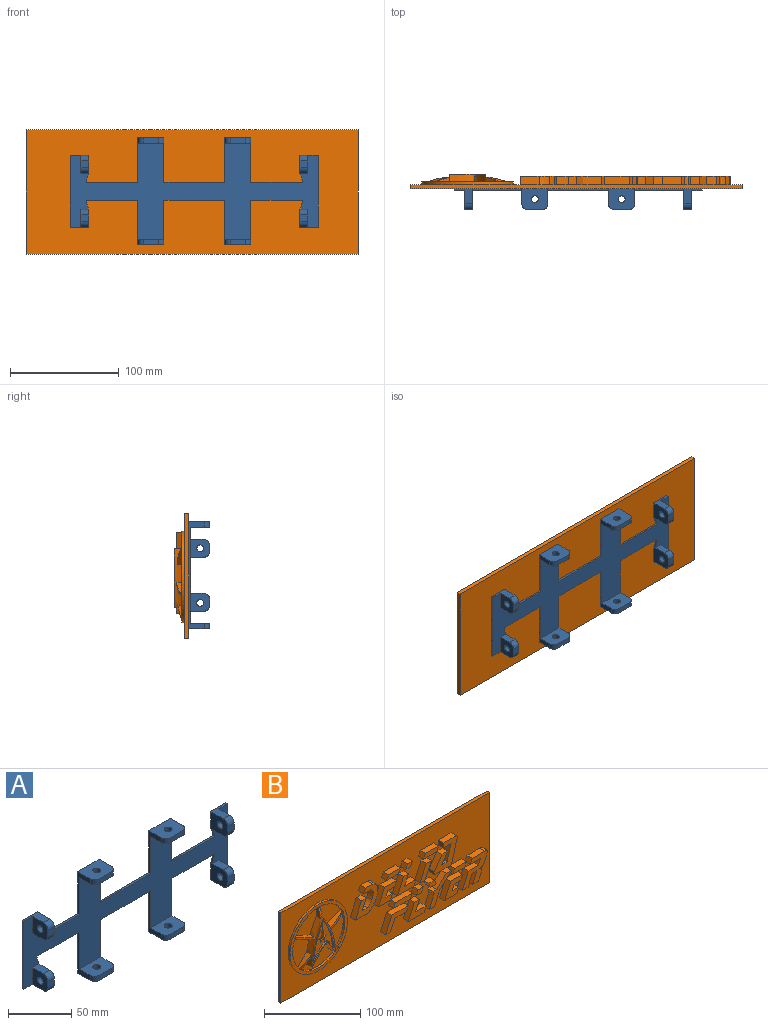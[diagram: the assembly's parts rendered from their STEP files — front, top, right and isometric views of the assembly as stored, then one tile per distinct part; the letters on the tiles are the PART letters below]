
ASSEMBLY  parts=2 mates=1
PART A: 78 faces, bbox 228.8x19.1x98.5 mm
  f0: plane 228.81x88.9mm, normal (0,-1,0), area 8492.5mm2, adj f1,f2,f3,f5,f6,f7,f9,f10
  f1: plane 40.81x13.97mm, normal (-1,0,0), area 131mm2, adj f0,f2,f34,f35,f36,f75
  f2: plane 47.52x1.78mm, normal (0,0,1), area 84.5mm2, adj f0,f1,f3,f35
  f3: cylinder r=50mm len=8.19mm, axis (0,1,0), area 15.1mm2, adj f0,f2,f4,f35
  f4: plane 19.05x16.45mm, normal (1,0,0), area 270.6mm2, adj f3,f5,f35,f45,f46,f57,f72,f73
  f5: plane 17.05x13.97mm, normal (0,0,1), area 116.4mm2, adj f0,f4,f6,f35,f44,f72
  f6: plane 66.15x1.78mm, normal (-1,0,0), area 117.6mm2, adj f0,f5,f7,f35
  f7: plane 17.05x13.97mm, normal (0,0,-1), area 116.4mm2, adj f0,f6,f8,f35,f48,f71
  f8: plane 19.05x16.45mm, normal (1,0,0), area 270.6mm2, adj f7,f9,f35,f47,f49,f56,f70,f71
  f9: cylinder r=50mm len=8.19mm, axis (0,1,0), area 15.1mm2, adj f0,f8,f10,f35
  f10: plane 47.52x1.78mm, normal (0,0,-1), area 84.5mm2, adj f0,f9,f11,f35
  f11: plane 40.81x13.97mm, normal (-1,0,0), area 131mm2, adj f0,f10,f12,f35,f38,f76
  f12: plane 24.02x19.05mm, normal (0,0,-1), area 414.8mm2, adj f11,f13,f35,f39,f60,f76,f77
  f13: plane 40.81x13.97mm, normal (1,0,0), area 131mm2, adj f0,f12,f14,f35,f38,f77
  f14: plane 55.89x1.78mm, normal (0,0,-1), area 99.4mm2, adj f0,f13,f15,f35
  f15: plane 40.81x13.97mm, normal (-1,0,0), area 131mm2, adj f0,f14,f16,f35,f40,f68
  f16: plane 24.02x19.05mm, normal (0,0,-1), area 414.8mm2, adj f15,f17,f35,f41,f59,f68,f69
  f17: plane 40.81x13.97mm, normal (1,0,0), area 131mm2, adj f0,f16,f18,f35,f40,f69
  f18: plane 47.77x1.78mm, normal (0,0,-1), area 84.9mm2, adj f0,f17,f19,f35
  f19: cylinder r=50mm len=8.19mm, axis (0,1,0), area 15.1mm2, adj f0,f18,f20,f35
  f20: plane 13.97x7.06mm, normal (0,0,1), area 86.5mm2, adj f0,f19,f21,f35,f52,f65
  f21: plane 19.05x16.45mm, normal (-1,0,0), area 270.6mm2, adj f20,f22,f35,f53,f54,f64,f65
  f22: plane 17.05x13.97mm, normal (0,0,-1), area 116.4mm2, adj f0,f21,f23,f35,f52,f64
  f23: plane 66.15x1.78mm, normal (1,0,0), area 117.6mm2, adj f0,f22,f24,f35
  f24: plane 17.05x13.97mm, normal (0,0,1), area 116.4mm2, adj f0,f23,f25,f35,f50,f62
  f25: plane 19.05x16.45mm, normal (-1,0,0), area 270.6mm2, adj f24,f26,f35,f51,f55,f62,f63
  f26: plane 13.97x7.06mm, normal (0,0,-1), area 86.5mm2, adj f0,f25,f27,f35,f50,f63
  f27: cylinder r=50mm len=8.19mm, axis (0,1,0), area 15.1mm2, adj f0,f26,f28,f35
  f28: plane 47.77x1.78mm, normal (0,0,1), area 84.9mm2, adj f0,f27,f29,f35
  f29: plane 40.81x13.97mm, normal (1,0,0), area 131mm2, adj f0,f28,f30,f35,f42,f66
  f30: plane 24.02x19.05mm, normal (0,0,1), area 414.8mm2, adj f29,f31,f35,f43,f58,f66,f67
  f31: plane 40.81x13.97mm, normal (-1,0,0), area 131mm2, adj f0,f30,f32,f35,f42,f67
  f32: plane 55.89x1.78mm, normal (0,0,1), area 99.4mm2, adj f0,f31,f33,f35
  f33: plane 40.81x13.97mm, normal (1,0,0), area 131mm2, adj f0,f32,f34,f35,f36,f74
  f34: plane 24.02x19.05mm, normal (0,0,1), area 414.8mm2, adj f1,f33,f35,f37,f61,f74,f75
  f35: plane 228.81x98.49mm, normal (0,1,0), area 9417.6mm2, adj f1,f2,f3,f4,f5,f6,f7,f8
  f36: plane 24.02x17.27mm, normal (0,0,-1), area 372.1mm2, adj f0,f1,f33,f37,f61,f74,f75
  f37: plane 13.86x4.8mm, normal (0,-1,0), area 66.5mm2, adj f34,f36,f74,f75
  f38: plane 24.02x17.27mm, normal (0,0,1), area 372.1mm2, adj f0,f11,f13,f39,f60,f76,f77
  f39: plane 13.86x4.8mm, normal (0,-1,0), area 66.5mm2, adj f12,f38,f76,f77
  f40: plane 24.02x17.27mm, normal (0,0,1), area 372.1mm2, adj f0,f15,f17,f41,f59,f68,f69
  f41: plane 13.86x4.8mm, normal (0,-1,0), area 66.5mm2, adj f16,f40,f68,f69
  f42: plane 24.02x17.27mm, normal (0,0,-1), area 372.1mm2, adj f0,f29,f31,f43,f58,f66,f67
  f43: plane 13.86x4.8mm, normal (0,-1,0), area 66.5mm2, adj f30,f42,f66,f67
  f44: plane 17.27x16.45mm, normal (-1,0,0), area 241.3mm2, adj f0,f5,f45,f46,f57,f72,f73
  f45: plane 12.19x7.06mm, normal (0,0,-1), area 86.1mm2, adj f0,f4,f44,f73
  f46: plane 7.06x6.29mm, normal (0,-1,0), area 44.4mm2, adj f4,f44,f72,f73
  f47: plane 12.19x7.06mm, normal (0,0,1), area 86.1mm2, adj f0,f8,f48,f70
  f48: plane 17.27x16.45mm, normal (-1,0,0), area 241.3mm2, adj f0,f7,f47,f49,f56,f70,f71
  f49: plane 7.06x6.29mm, normal (0,-1,0), area 44.4mm2, adj f8,f48,f70,f71
  f50: plane 17.27x16.45mm, normal (1,0,0), area 241.3mm2, adj f0,f24,f26,f51,f55,f62,f63
  f51: plane 7.06x6.29mm, normal (0,-1,0), area 44.4mm2, adj f25,f50,f62,f63
  f52: plane 17.27x16.45mm, normal (1,0,0), area 241.3mm2, adj f0,f20,f22,f53,f54,f64,f65
  f53: plane 7.06x6.29mm, normal (0,-1,0), area 44.4mm2, adj f21,f52,f64,f65
  f54: cylinder r=3.17mm len=7.06mm, axis (1,0,0), area 140.8mm2, adj f21,f52
  f55: cylinder r=3.17mm len=7.06mm, axis (1,0,0), area 140.8mm2, adj f25,f50
  f56: cylinder r=3.17mm len=7.06mm, axis (1,0,0), area 140.8mm2, adj f8,f48
  f57: cylinder r=3.17mm len=7.06mm, axis (1,0,0), area 140.8mm2, adj f4,f44
  f58: cylinder r=3.17mm len=6.35mm, axis (0,0,-1), area 95.7mm2, adj f30,f42
  f59: cylinder r=3.17mm len=6.35mm, axis (0,0,-1), area 95.7mm2, adj f16,f40
  f60: cylinder r=3.17mm len=6.35mm, axis (0,0,-1), area 95.7mm2, adj f12,f38
  f61: cylinder r=3.17mm len=6.35mm, axis (0,0,-1), area 95.7mm2, adj f34,f36
  f62: cylinder r=5.08mm len=7.06mm, axis (1,0,0), area 56.3mm2, adj f24,f25,f50,f51
  f63: cylinder r=5.08mm len=7.06mm, axis (-1,0,0), area 56.3mm2, adj f25,f26,f50,f51
  f64: cylinder r=5.08mm len=7.06mm, axis (-1,0,0), area 56.3mm2, adj f21,f22,f52,f53
  f65: cylinder r=5.08mm len=7.06mm, axis (1,0,0), area 56.3mm2, adj f20,f21,f52,f53
  f66: cylinder r=5.08mm len=5.08mm, axis (0,0,-1), area 38.3mm2, adj f29,f30,f42,f43
  f67: cylinder r=5.08mm len=5.08mm, axis (0,0,1), area 38.3mm2, adj f30,f31,f42,f43
  f68: cylinder r=5.08mm len=5.08mm, axis (0,0,1), area 38.3mm2, adj f15,f16,f40,f41
  f69: cylinder r=5.08mm len=5.08mm, axis (0,0,-1), area 38.3mm2, adj f16,f17,f40,f41
  f70: cylinder r=5.08mm len=7.06mm, axis (1,0,0), area 56.3mm2, adj f8,f47,f48,f49
  f71: cylinder r=5.08mm len=7.06mm, axis (-1,0,0), area 56.3mm2, adj f7,f8,f48,f49
  f72: cylinder r=5.08mm len=7.06mm, axis (1,0,0), area 56.3mm2, adj f4,f5,f44,f46
  f73: cylinder r=5.08mm len=7.06mm, axis (-1,0,0), area 56.3mm2, adj f4,f44,f45,f46
  f74: cylinder r=5.08mm len=5.08mm, axis (0,0,-1), area 38.3mm2, adj f33,f34,f36,f37
  f75: cylinder r=5.08mm len=5.08mm, axis (0,0,1), area 38.3mm2, adj f1,f34,f36,f37
  f76: cylinder r=5.08mm len=5.08mm, axis (0,0,1), area 38.3mm2, adj f11,f12,f38,f39
  f77: cylinder r=5.08mm len=5.08mm, axis (0,0,-1), area 38.3mm2, adj f12,f13,f38,f39
PART B: 198 faces, bbox 307.6x15x116 mm
  f0: plane 7.13x0.2mm, normal (-0.71,0,0.7), area 2mm2, adj f1,f14,f21,f181
  f1: plane 7.3x2.89mm, normal (-0.7,0,-0.71), area 28.9mm2, adj f0,f14,f21,f181
  f2: plane 10.27x10.11mm, normal (-0.7,0,-0.71), area 73mm2, adj f14,f22,f23,f174,f179
  f3: plane 12.48x12.3mm, normal (0.7,0,0.71), area 91.2mm2, adj f15,f22,f23,f31,f179
  f4: plane 23.9x11.42mm, normal (-0.41,0,0.91), area 146.5mm2, adj f16,f20,f24,f30,f179
  f5: plane 23.28x10.7mm, normal (0.41,0,-0.91), area 148mm2, adj f15,f20,f24,f31,f179
  f6: plane 12.38x6.44mm, normal (-1,0,0), area 60.4mm2, adj f12,f19,f25,f29,f178
  f7: plane 12.02x6.38mm, normal (1,0,0), area 58.2mm2, adj f16,f19,f25,f30,f179
  f8: plane 25.58x12.34mm, normal (0.41,0,0.91), area 157.2mm2, adj f12,f18,f26,f29,f178
  f9: plane 24.74x11.38mm, normal (-0.41,0,-0.91), area 159.1mm2, adj f13,f18,f26,f28,f178
  f10: plane 11.54x11.37mm, normal (0.7,0,-0.71), area 84.4mm2, adj f14,f17,f27,f174,f178
  f11: plane 14.14x13.93mm, normal (-0.7,0,0.71), area 105.9mm2, adj f13,f17,f27,f28,f178
  f12: plane 32.85x31.32mm, normal (0,-1,0), area 607.9mm2, adj f6,f8,f29,f178
  f13: plane 40.92x27.38mm, normal (0,-1,0), area 711.6mm2, adj f9,f11,f28,f178
  f14: plane 54.07x32.14mm, normal (0,-1,0), area 954.8mm2, adj f0,f1,f2,f10,f174,f178,f179,f181
  f15: plane 40.92x25.98mm, normal (0,-1,0), area 683.9mm2, adj f3,f5,f31,f179
  f16: plane 32.85x30.71mm, normal (0,-1,0), area 587.5mm2, adj f4,f7,f30,f179
  f17: revolved ~16.37x15.22mm, area 45.6mm2, adj f10,f11,f27,f178
  f18: revolved ~25.12x16.72mm, area 72.4mm2, adj f8,f9,f26,f178
  f19: revolved ~12.24x3.4mm, area 27.6mm2, adj f6,f7,f25,f178,f179
  f20: revolved ~23.71x15.5mm, area 65.7mm2, adj f4,f5,f24,f179
  f21: revolved ~3.16x3.11mm, area 1mm2, adj f0,f1,f181
  f22: revolved ~14.64x13.71mm, area 39.9mm2, adj f2,f3,f23,f179
  f23: cylinder r=38.27mm len=1.73mm, axis (0,1,0), area 1.7mm2, adj f2,f3,f22,f176
  f24: cylinder r=38.27mm len=1.99mm, axis (0,1,0), area 1.5mm2, adj f4,f5,f20,f176
  f25: cylinder r=38.27mm len=2.33mm, axis (0,1,0), area 1.6mm2, adj f6,f7,f19,f176
  f26: cylinder r=38.27mm len=1.99mm, axis (0,1,0), area 1.5mm2, adj f8,f9,f18,f176
  f27: cylinder r=38.27mm len=1.73mm, axis (0,1,0), area 1.7mm2, adj f10,f11,f17,f176
  f28: cylinder r=38.27mm len=40.92mm, axis (0,1,0), area 111.1mm2, adj f9,f11,f13,f176
  f29: cylinder r=38.27mm len=32.85mm, axis (0,1,0), area 103.4mm2, adj f6,f8,f12,f176
  f30: cylinder r=38.27mm len=32.85mm, axis (0,1,0), area 103.4mm2, adj f4,f7,f16,f176
  f31: cylinder r=38.27mm len=40.92mm, axis (0,1,0), area 111.1mm2, adj f3,f5,f15,f176
  f32: plane 305.88x114.33mm, normal (0,-1,0), area 25337.4mm2, adj f33,f34,f35,f36,f38,f39,f40,f41
  f33: plane 305.88x3.81mm, normal (0,0,-1), area 1165.4mm2, adj f32,f34,f36,f37
  f34: plane 114.33x3.81mm, normal (1,0,0), area 435.6mm2, adj f32,f33,f35,f37
  f35: plane 305.88x3.81mm, normal (0,0,1), area 1165.4mm2, adj f32,f34,f36,f37
  f36: plane 114.33x3.81mm, normal (-1,0,0), area 435.6mm2, adj f32,f33,f35,f37
  f37: plane 305.88x114.33mm, normal (0,1,0), area 34972.4mm2, adj f33,f34,f35,f36
  f38: plane 17.61x7.62mm, normal (0,0,1), area 134.2mm2, adj f32,f39,f41,f42
  f39: plane 7.62x6.1mm, normal (-0.92,0,0.4), area 50.6mm2, adj f32,f38,f40,f42
  f40: plane 17.61x7.62mm, normal (0,0,-1), area 134.2mm2, adj f32,f39,f41,f42
  f41: plane 7.62x6.1mm, normal (0.92,0,-0.4), area 50.6mm2, adj f32,f38,f40,f42
  f42: plane 20.23x6.1mm, normal (0,-1,0), area 107.4mm2, adj f38,f39,f40,f41
  f43: plane 7.62x3.65mm, normal (-1,0,0), area 27.8mm2, adj f32,f44,f54,f55
  f44: plane 24.88x7.62mm, normal (0,0,-1), area 189.6mm2, adj f32,f43,f45,f55
  f45: plane 31.45x9.07mm, normal (0.96,0,-0.28), area 249.4mm2, adj f32,f44,f46,f55
  f46: plane 7.62x2.08mm, normal (0.74,0,0.67), area 21.4mm2, adj f32,f45,f47,f55
  f47: plane 18.96x7.62mm, normal (0,0,1), area 144.4mm2, adj f32,f46,f48,f55
  f48: plane 7.62x6.1mm, normal (-1,0,0), area 46.5mm2, adj f32,f47,f49,f55
  f49: plane 11.34x7.62mm, normal (0,0,-1), area 86.4mm2, adj f32,f48,f50,f55
  f50: plane 20.32x7.62mm, normal (-0.96,0,0.28), area 161.2mm2, adj f32,f49,f51,f55
  f51: plane 7.67x7.62mm, normal (0,0,1), area 58.5mm2, adj f32,f50,f52,f55
  f52: plane 13.21x8.8mm, normal (0.83,0,-0.55), area 120.9mm2, adj f32,f51,f53,f55
  f53: plane 8.61x7.62mm, normal (0,0,1), area 65.6mm2, adj f32,f52,f54,f55
  f54: plane 16.67x11.1mm, normal (-0.83,0,0.55), area 152.6mm2, adj f32,f43,f53,f55
  f55: plane 33.95x33.53mm, normal (0,-1,0), area 586.2mm2, adj f43,f44,f45,f46,f47,f48,f49,f50
  f56: plane 19.44x7.62mm, normal (0,0,1), area 148.2mm2, adj f32,f57,f59,f60
  f57: plane 7.62x6.1mm, normal (-0.92,0,0.4), area 50.6mm2, adj f32,f56,f58,f60
  f58: plane 19.44x7.62mm, normal (0,0,-1), area 148.2mm2, adj f32,f57,f59,f60
  f59: plane 7.62x6.1mm, normal (0.92,0,-0.4), area 50.6mm2, adj f32,f56,f58,f60
  f60: plane 22.07x6.1mm, normal (0,-1,0), area 118.5mm2, adj f56,f57,f58,f59
  f61: plane 7.62x7.14mm, normal (0,0,1), area 54.4mm2, adj f32,f62,f64,f65
  f62: plane 7.62x6.1mm, normal (-0.92,0,0.4), area 50.6mm2, adj f32,f61,f63,f65
  f63: plane 7.62x7.14mm, normal (0,0,-1), area 54.4mm2, adj f32,f62,f64,f65
  f64: plane 7.62x6.1mm, normal (0.92,0,-0.4), area 50.6mm2, adj f32,f61,f63,f65
  f65: plane 9.76x6.1mm, normal (0,-1,0), area 43.5mm2, adj f61,f62,f63,f64
  f66: plane 7.62x6.92mm, normal (0,0,1), area 52.7mm2, adj f32,f67,f81,f82
  f67: plane 20.32x8.74mm, normal (-0.92,0,0.4), area 168.6mm2, adj f32,f66,f68,f82
  f68: plane 17.24x7.62mm, normal (0,0,-1), area 131.3mm2, adj f32,f67,f69,f82
  f69: extruded ~9.81x7.62mm, area 94.3mm2, adj f32,f68,f70,f82
  f70: extruded ~7.62x7.11mm, area 62.7mm2, adj f32,f69,f71,f82
  f71: extruded ~7.62x6.1mm, area 48.1mm2, adj f32,f70,f72,f82
  f72: extruded ~7.62x7.11mm, area 55mm2, adj f32,f71,f73,f82
  f73: extruded ~7.62x7.25mm, area 75.4mm2, adj f32,f72,f74,f82
  f74: plane 10.32x7.62mm, normal (0,0,1), area 78.6mm2, adj f32,f73,f75,f82
  f75: plane 7.62x6.1mm, normal (-0.92,0,0.4), area 50.6mm2, adj f32,f74,f76,f82
  f76: plane 10.59x7.62mm, normal (0,0,-1), area 80.7mm2, adj f32,f75,f77,f82
  f77: extruded ~7.62x7.11mm, area 65.3mm2, adj f32,f76,f78,f82
  f78: extruded ~7.62x6.1mm, area 49mm2, adj f32,f77,f79,f82
  f79: extruded ~7.62x7.11mm, area 77.4mm2, adj f32,f78,f80,f82
  f80: plane 7.62x7.15mm, normal (0,0,1), area 54.5mm2, adj f32,f79,f81,f82
  f81: plane 13.21x7.62mm, normal (0.92,0,-0.4), area 109.6mm2, adj f32,f66,f80,f82
  f82: plane 33.53x32.87mm, normal (0,-1,0), area 497.5mm2, adj f66,f67,f68,f69,f70,f71,f72,f73
  f83: plane 7.62x7.11mm, normal (0.92,0,-0.4), area 59mm2, adj f32,f84,f90,f91
  f84: plane 9.89x7.62mm, normal (0,0,-1), area 75.4mm2, adj f32,f83,f85,f91
  f85: plane 7.62x6.1mm, normal (0.92,0,-0.4), area 50.6mm2, adj f32,f84,f86,f91
  f86: plane 17.61x7.62mm, normal (0,0,1), area 134.2mm2, adj f32,f85,f87,f91
  f87: plane 20.32x8.74mm, normal (-0.92,0,0.4), area 168.6mm2, adj f32,f86,f88,f91
  f88: plane 17.61x7.62mm, normal (0,0,-1), area 134.2mm2, adj f32,f87,f89,f91
  f89: plane 7.62x7.11mm, normal (0.92,0,-0.4), area 59mm2, adj f32,f88,f90,f91
  f90: plane 9.89x7.62mm, normal (0,0,1), area 75.4mm2, adj f32,f83,f89,f91
  f91: plane 26.35x20.32mm, normal (0,-1,0), area 287.5mm2, adj f83,f84,f85,f86,f87,f88,f89,f90
  f92: plane 7.62x7.53mm, normal (0,0,1), area 57.4mm2, adj f32,f93,f95,f96
  f93: plane 20.32x8.74mm, normal (-0.92,0,0.4), area 168.6mm2, adj f32,f92,f94,f96
  f94: plane 7.62x7.53mm, normal (0,0,-1), area 57.4mm2, adj f32,f93,f95,f96
  f95: plane 20.32x8.74mm, normal (0.92,0,-0.4), area 168.6mm2, adj f32,f92,f94,f96
  f96: plane 20.32x16.27mm, normal (0,-1,0), area 153.1mm2, adj f92,f93,f94,f95
  f97: plane 7.62x7.14mm, normal (0,0,1), area 54.4mm2, adj f32,f98,f102,f103
  f98: plane 20.32x8.74mm, normal (-0.92,0,0.4), area 168.6mm2, adj f32,f97,f99,f103
  f99: plane 23.73x7.62mm, normal (0,0,-1), area 180.8mm2, adj f32,f98,f100,f103
  f100: plane 7.62x7.11mm, normal (0.92,0,-0.4), area 59mm2, adj f32,f99,f101,f103
  f101: plane 16.59x7.62mm, normal (0,0,1), area 126.4mm2, adj f32,f100,f102,f103
  f102: plane 13.21x7.62mm, normal (0.92,0,-0.4), area 109.6mm2, adj f32,f97,f101,f103
  f103: plane 26.79x20.32mm, normal (0,-1,0), area 263mm2, adj f97,f98,f99,f100,f101,f102
  f104: plane 17.6x7.62mm, normal (0,0,1), area 134.1mm2, adj f32,f105,f107,f108
  f105: plane 7.62x6.1mm, normal (-0.92,0,0.4), area 50.6mm2, adj f32,f104,f106,f108
  f106: plane 17.6x7.62mm, normal (0,0,-1), area 134.1mm2, adj f32,f105,f107,f108
  f107: plane 7.62x6.1mm, normal (0.92,0,-0.4), area 50.6mm2, adj f32,f104,f106,f108
  f108: plane 20.22x6.1mm, normal (0,-1,0), area 107.3mm2, adj f104,f105,f106,f107
  f109: plane 24.26x7.62mm, normal (0,0,1), area 184.9mm2, adj f32,f110,f112,f113
  f110: plane 7.62x6.1mm, normal (-0.92,0,0.4), area 50.6mm2, adj f32,f109,f111,f113
  f111: plane 24.26x7.62mm, normal (0,0,-1), area 184.9mm2, adj f32,f110,f112,f113
  f112: plane 7.62x6.1mm, normal (0.92,0,-0.4), area 50.6mm2, adj f32,f109,f111,f113
  f113: plane 26.89x6.1mm, normal (0,-1,0), area 147.9mm2, adj f109,f110,f111,f112
  f114: plane 8.43x7.62mm, normal (0,0,1), area 64.2mm2, adj f32,f115,f117,f118
  f115: plane 7.62x6.1mm, normal (-0.91,0,-0.43), area 51.3mm2, adj f32,f114,f116,f118
  f116: plane 8.43x7.62mm, normal (0,0,-1), area 64.2mm2, adj f32,f115,f117,f118
  f117: plane 7.62x6.1mm, normal (0.91,0,0.43), area 51.3mm2, adj f32,f114,f116,f118
  f118: plane 11.29x6.1mm, normal (0,-1,0), area 51.4mm2, adj f114,f115,f116,f117
  f119: plane 14.22x7.62mm, normal (0.92,0,-0.4), area 118mm2, adj f32,f120,f135,f136
  f120: plane 7.62x6.68mm, normal (0,0,-1), area 50.9mm2, adj f32,f119,f121,f136
  f121: plane 14.22x7.62mm, normal (-0.92,0,0.4), area 118mm2, adj f32,f120,f122,f136
  f122: plane 8.72x7.62mm, normal (0,0,-1), area 66.4mm2, adj f32,f121,f123,f136
  f123: plane 7.62x7.11mm, normal (0.92,0,-0.4), area 59mm2, adj f32,f122,f124,f136
  f124: extruded ~7.62x7.11mm, area 58.6mm2, adj f32,f123,f125,f136
  f125: extruded ~7.62x1.58mm, area 14.4mm2, adj f32,f124,f126,f136
  f126: extruded ~7.62x7.03mm, area 71.7mm2, adj f32,f125,f127,f136
  f127: plane 8.16x7.62mm, normal (0.92,0,-0.4), area 67.7mm2, adj f32,f126,f128,f136
  f128: extruded ~7.62x5.05mm, area 63.9mm2, adj f32,f127,f129,f136
  f129: plane 18.35x7.62mm, normal (0,0,1), area 139.8mm2, adj f32,f128,f130,f136
  f130: plane 7.62x6.1mm, normal (-0.92,0,0.4), area 50.6mm2, adj f32,f129,f131,f136
  f131: plane 15.04x7.62mm, normal (0,0,-1), area 114.6mm2, adj f32,f130,f132,f136
  f132: plane 7.62x7.11mm, normal (-0.92,0,0.4), area 59mm2, adj f32,f131,f133,f136
  f133: plane 15.04x7.62mm, normal (0,0,1), area 114.6mm2, adj f32,f132,f134,f136
  f134: plane 20.32x8.74mm, normal (-0.92,0,0.4), area 168.6mm2, adj f32,f133,f135,f136
  f135: plane 8.36x7.62mm, normal (0,0,-1), area 63.7mm2, adj f32,f119,f134,f136
  f136: plane 36.82x33.53mm, normal (0,-1,0), area 578.4mm2, adj f119,f120,f121,f122,f123,f124,f125,f126
  f137: plane 7.62x7.53mm, normal (0,0,1), area 57.4mm2, adj f32,f138,f140,f141
  f138: plane 7.62x6.1mm, normal (-0.92,0,0.4), area 50.6mm2, adj f32,f137,f139,f141
  f139: plane 7.62x7.53mm, normal (0,0,-1), area 57.4mm2, adj f32,f138,f140,f141
  f140: plane 7.62x6.1mm, normal (0.92,0,-0.4), area 50.6mm2, adj f32,f137,f139,f141
  f141: plane 10.16x6.1mm, normal (0,-1,0), area 45.9mm2, adj f137,f138,f139,f140
  f142: plane 20.32x8.74mm, normal (-0.92,0,0.4), area 168.6mm2, adj f32,f143,f149,f150
  f143: plane 17.6x7.62mm, normal (0,0,-1), area 134.1mm2, adj f32,f142,f144,f150
  f144: plane 7.62x7.11mm, normal (0.92,0,-0.4), area 59mm2, adj f32,f143,f145,f150
  f145: plane 9.93x7.62mm, normal (0,0,1), area 75.6mm2, adj f32,f144,f146,f150
  f146: plane 7.62x7.11mm, normal (0.92,0,-0.4), area 59mm2, adj f32,f145,f147,f150
  f147: plane 9.93x7.62mm, normal (0,0,-1), area 75.6mm2, adj f32,f146,f148,f150
  f148: plane 7.62x6.1mm, normal (0.92,0,-0.4), area 50.6mm2, adj f32,f147,f149,f150
  f149: plane 17.6x7.62mm, normal (0,0,1), area 134.1mm2, adj f32,f142,f148,f150
  f150: plane 26.34x20.32mm, normal (0,-1,0), area 287mm2, adj f142,f143,f144,f145,f146,f147,f148,f149
  f151: plane 24.26x7.62mm, normal (0,0,1), area 184.9mm2, adj f32,f152,f156,f157
  f152: plane 20.32x8.74mm, normal (-0.92,0,0.4), area 168.6mm2, adj f32,f151,f153,f157
  f153: plane 7.62x7.14mm, normal (0,0,-1), area 54.4mm2, adj f32,f152,f154,f157
  f154: plane 14.22x7.62mm, normal (0.92,0,-0.4), area 118mm2, adj f32,f153,f155,f157
  f155: plane 17.13x7.62mm, normal (0,0,-1), area 130.5mm2, adj f32,f154,f156,f157
  f156: plane 7.62x6.1mm, normal (0.92,0,-0.4), area 50.6mm2, adj f32,f151,f155,f157
  f157: plane 33x20.32mm, normal (0,-1,0), area 249.4mm2, adj f151,f152,f153,f154,f155,f156
  f158: plane 23x7.62mm, normal (0,0,-1), area 175.3mm2, adj f32,f159,f163,f164
  f159: plane 7.62x7.11mm, normal (0.92,0,-0.4), area 59mm2, adj f32,f158,f160,f164
  f160: plane 15.47x7.62mm, normal (0,0,1), area 117.9mm2, adj f32,f159,f161,f164
  f161: plane 13.21x7.62mm, normal (0.92,0,-0.4), area 109.6mm2, adj f32,f160,f162,f164
  f162: plane 7.62x7.53mm, normal (0,0,1), area 57.4mm2, adj f32,f161,f163,f164
  f163: plane 20.32x8.74mm, normal (-0.92,0,0.4), area 168.6mm2, adj f32,f158,f162,f164
  f164: plane 26.06x20.32mm, normal (0,-1,0), area 263.1mm2, adj f158,f159,f160,f161,f162,f163
  f165: plane 8.06x7.62mm, normal (0,0,1), area 61.4mm2, adj f32,f166,f172,f173
  f166: plane 14.05x13.21mm, normal (-0.68,0,0.73), area 147mm2, adj f32,f165,f167,f173
  f167: plane 7.62x5.45mm, normal (0,0,1), area 41.5mm2, adj f32,f166,f168,f173
  f168: plane 7.62x3.97mm, normal (-0.91,0,-0.43), area 33.5mm2, adj f32,f167,f169,f173
  f169: plane 16.35x7.62mm, normal (-0.92,0,0.4), area 135.6mm2, adj f32,f168,f170,f173
  f170: plane 7.62x7.41mm, normal (0,0,-1), area 56.5mm2, adj f32,f169,f171,f173
  f171: plane 16.35x7.62mm, normal (0.92,0,-0.4), area 135.6mm2, adj f32,f170,f172,f173
  f172: plane 18.28x17.18mm, normal (0.68,0,-0.73), area 191.2mm2, adj f32,f165,f171,f173
  f173: plane 33.53x32.73mm, normal (0,-1,0), area 269.2mm2, adj f165,f166,f167,f168,f169,f170,f171,f172
  f174: cylinder r=38.27mm len=54.07mm, axis (0,1,0), area 152.5mm2, adj f2,f10,f14,f176
  f175: cylinder r=42.14mm len=84.28mm, axis (0,1,0), area 672.5mm2, adj f32,f176
  f176: plane 84.28x84.28mm, normal (0,-1,0), area 977.3mm2, adj f23,f24,f25,f26,f27,f28,f29,f30
  f177: cylinder r=108.93mm len=46.03mm, axis (0,1,0), area 91.7mm2, adj f180,f182,f183,f186
  f178: cylinder r=110.65mm len=54.01mm, axis (0,1,0), area 484.7mm2, adj f6,f8,f9,f10,f11,f12,f13,f14
  f179: cylinder r=82.07mm len=51.47mm, axis (0,1,0), area 471.7mm2, adj f2,f3,f4,f5,f7,f14,f15,f16
  f180: cylinder r=80.35mm len=42.3mm, axis (0,1,0), area 101.8mm2, adj f177,f182,f183,f184,f185,f186
  f181: extruded ~33.68x19.86mm, area 457.8mm2, adj f0,f1,f14,f21,f178,f179,f183
  f182: extruded ~29.8x16.4mm, area 116.5mm2, adj f177,f180,f183,f184,f185,f186
  f183: plane 54.01x33.69mm, normal (0,-1,0), area 248.3mm2, adj f177,f178,f179,f180,f181,f182
  f184: plane 7.6x2.09mm, normal (-0.7,0,-0.71), area 22.3mm2, adj f180,f182,f185,f186
  f185: plane 4.23x2.27mm, normal (0,-1,0), area 2mm2, adj f180,f182,f184
  f186: plane 46.03x29.64mm, normal (0,-1,0), area 528.4mm2, adj f177,f180,f182,f184,f187,f188,f189,f190
  f187: plane 4.16x3.18mm, normal (-0.16,0,-0.99), area 13.4mm2, adj f186,f188,f196,f197
  f188: plane 13.57x3.18mm, normal (-0.99,0,-0.15), area 43.6mm2, adj f186,f187,f189,f197
  f189: plane 13.47x3.18mm, normal (0.99,0,-0.11), area 43mm2, adj f186,f188,f190,f197
  f190: plane 4.56x3.18mm, normal (0.2,0,-0.98), area 14.8mm2, adj f186,f189,f191,f197
  f191: plane 3.77x3.18mm, normal (0.43,0,0.9), area 13.3mm2, adj f186,f190,f192,f197
  f192: plane 3.99x3.18mm, normal (0.97,0,-0.23), area 13mm2, adj f186,f191,f193,f197
  f193: plane 3.34x3.18mm, normal (-0.63,0,0.77), area 13.7mm2, adj f186,f192,f194,f197
  f194: plane 3.26x3.18mm, normal (0.66,0,0.75), area 13.7mm2, adj f186,f193,f195,f197
  f195: plane 4.19x3.18mm, normal (-0.98,0,-0.18), area 13.5mm2, adj f186,f194,f196,f197
  f196: plane 3.56x3.18mm, normal (-0.46,0,0.89), area 12.7mm2, adj f186,f187,f195,f197
  f197: plane 20.27x12.21mm, normal (0,-1,0), area 59.7mm2, adj f187,f188,f189,f190,f191,f192,f193,f194
PLACE A t=(0,0.16,0)mm
PLACE B rot(axis=(1,0,0),180deg) t=(-2.58,3.97,-1.23)mm
MATE planar B.f37 <-> A.f3  axis (0,-1,0) through (-2.1,0.16,-0.34)mm
